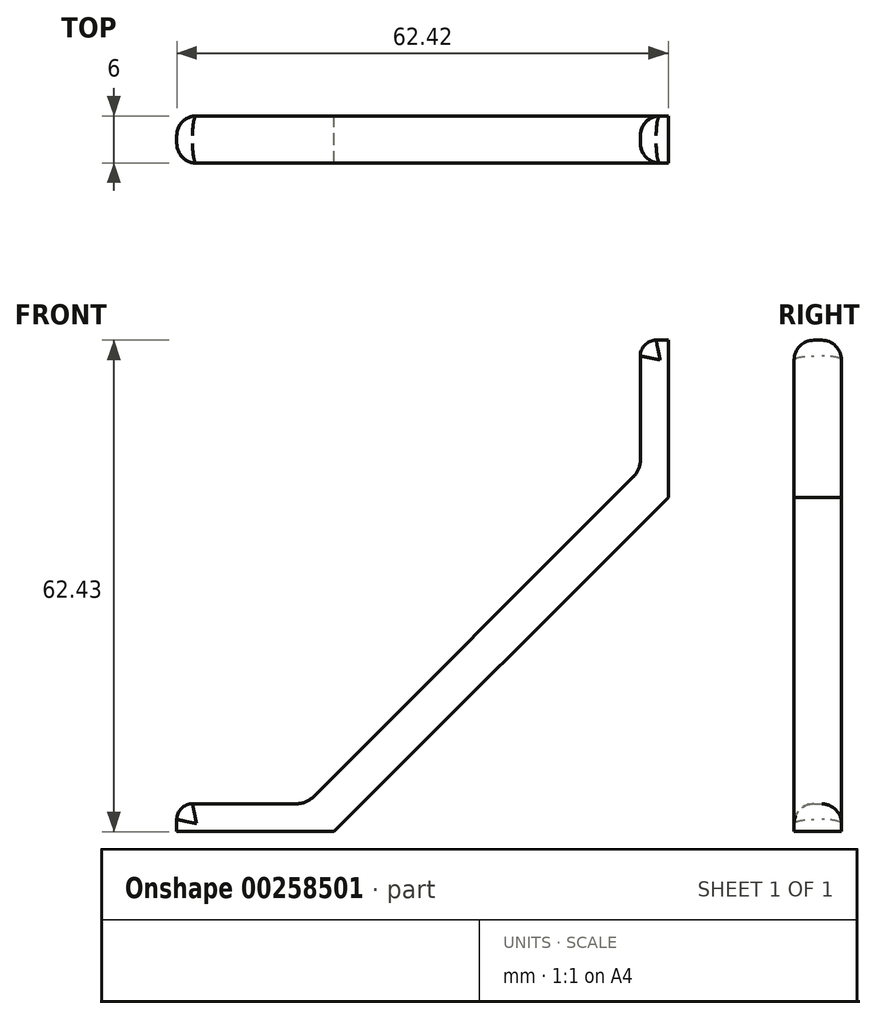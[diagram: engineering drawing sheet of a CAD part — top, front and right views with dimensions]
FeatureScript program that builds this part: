
annotation { "Feature Type Name" : "Feature", "Feature Type Description" : "" }
export const myFeature = defineFeature(function(context is Context, id is Id, definition is map)
    precondition{}
    {
        {
            var Q0;
            Q0=qCreatedBy(makeId("Front.planeOp"),FACE);
            var sketch = newSketch(context, id + "F0", { "sketchPlane" : qUnion([Q0])});
            skLineSegment(sketch, "E0", {"start": v(0.88, 0.88) * mm, "end": v(41.55, 41.55) * mm});
            skLineSegment(sketch, "E1", {"start": v(0, 0) * mm, "end": v(0, 60.66) * mm, "construction": true});
            skLineSegment(sketch, "E2", {"start": v(0, 0) * mm, "end": v(22.94, -22.94) * mm, "construction": true});
            skPoint(sketch, "E3", {"position": v(3.54, -3.54) * mm});
            skLineSegment(sketch, "E4", {"start": v(3.54, -3.54) * mm, "end": v(45.96, 38.9) * mm});
            skLineSegment(sketch, "E5", {"start": v(3.54, -3.54) * mm, "end": v(-16.46, -3.54) * mm});
            skLineSegment(sketch, "E6", {"start": v(-16.46, -3.54) * mm, "end": v(-16.46, -2) * mm});
            skLineSegment(sketch, "E7", {"start": v(-14.46, 0) * mm, "end": v(-1.24, 0) * mm});
            skPoint(sketch, "E8.visualSharp", {"position": v(-16.46, 0) * mm});
            skArc(sketch, "E8.filletArc", {"start": v(-14.46, 0) * mm, "mid": v(-15.88, -0.59) * mm, "end": v(-16.46, -2) * mm});
            skPoint(sketch, "E9.visualSharp", {"position": v(0, 0) * mm});
            skArc(sketch, "E9.filletArc", {"start": v(-1.24, 0) * mm, "mid": v(-0.1, 0.23) * mm, "end": v(0.88, 0.88) * mm});
            skLineSegment(sketch, "E10.filletArc", {"start": v(3.54, -3.54) * mm, "end": v(3.54, -3.54) * mm});
            skLineSegment(sketch, "E11", {"start": v(45.96, 38.9) * mm, "end": v(45.96, 58.9) * mm});
            skLineSegment(sketch, "E12", {"start": v(42.43, 43.67) * mm, "end": v(42.43, 56.9) * mm});
            skLineSegment(sketch, "E13", {"start": v(44.43, 58.9) * mm, "end": v(45.96, 58.9) * mm});
            skPoint(sketch, "E14.visualSharp", {"position": v(42.43, 58.9) * mm});
            skArc(sketch, "E14.filletArc", {"start": v(44.43, 58.9) * mm, "mid": v(43.01, 58.3) * mm, "end": v(42.43, 56.9) * mm});
            skPoint(sketch, "E15.visualSharp", {"position": v(45.96, 38.9) * mm});
            skLineSegment(sketch, "E15.filletArc", {"start": v(45.96, 38.9) * mm, "end": v(45.96, 38.9) * mm});
            skPoint(sketch, "E16.visualSharp", {"position": v(42.43, 42.43) * mm});
            skArc(sketch, "E16.filletArc", {"start": v(41.55, 41.55) * mm, "mid": v(42.2, 42.52) * mm, "end": v(42.43, 43.67) * mm});
            skSolve(sketch);
        }
        {
            var Q0;
            Q0=makeQuery(id+"F0.imprint","IMPRINT",FACE,{"disambiguationData":[TD([[makeQuery(id+"F0.imprint","IMPRINT",EDGE,{"derivedFrom":sQuery(id+"F0.wireOp",EDGE,"E0")}),-1.0]])]});
            extrude(context, id + "F1", {"entities" : qUnion([Q0]), "depth" : 6 * mm});
        }
        {
            var Q0;
            Q0=makeQuery(id+"F1.opExtrude","CAP_EDGE",EDGE,{"disambiguationData":[OSD([sQuery(id+"F0.wireOp",EDGE,"E0")])],"isStart":false});
            var Q1;
            Q1=makeQuery(id+"F1.opExtrude","CAP_EDGE",EDGE,{"disambiguationData":[OSD([sQuery(id+"F0.wireOp",EDGE,"E0")])],"isStart":true});
            fillet(context, id + "F2", {"entities" : qUnion([Q0, Q1]), "radius" : 2.5 * mm, "tangentPropagation" : true, "allowEdgeOverflow" : false});
        }
    });
